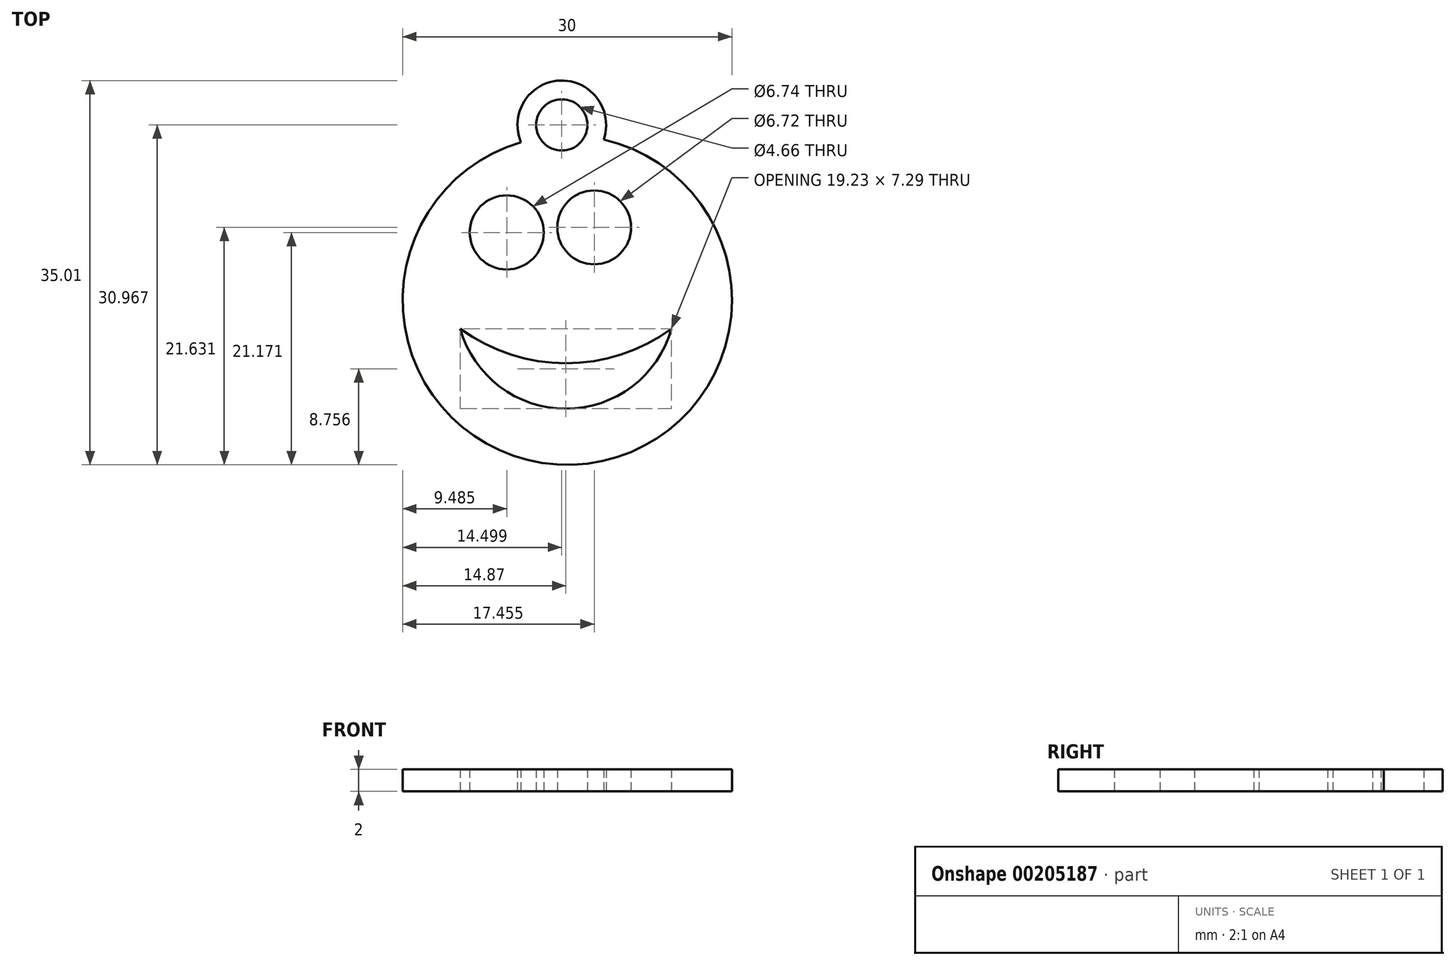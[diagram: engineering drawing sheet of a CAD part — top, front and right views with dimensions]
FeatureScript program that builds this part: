
annotation { "Feature Type Name" : "Feature", "Feature Type Description" : "" }
export const myFeature = defineFeature(function(context is Context, id is Id, definition is map)
    precondition{}
    {
        {
            var Q0;
            Q0=qCreatedBy(makeId("Top.planeOp"),FACE);
            var sketch = newSketch(context, id + "F0", { "sketchPlane" : qUnion([Q0])});
            skArc(sketch, "E0", {"start": v(-4.22, 14.4) * mm, "mid": v(0.47, -15) * mm, "end": v(3.31, 14.63) * mm});
            skArc(sketch, "E1", {"start": v(-9.75, -2.6) * mm, "mid": v(-0.13, -9.89) * mm, "end": v(9.49, -2.6) * mm});
            skArc(sketch, "E2", {"start": v(-9.75, -2.6) * mm, "mid": v(-0.13, -5.75) * mm, "end": v(9.49, -2.6) * mm});
            skCircle(sketch, "E3", {"center": v(-5.52, 6.17) * mm, "radius": 3.37 * mm});
            skCircle(sketch, "E4", {"center": v(2.46, 6.63) * mm, "radius": 3.36 * mm});
            skArc(sketch, "E5", {"start": v(3.31, 14.63) * mm, "mid": v(-0.63, 20) * mm, "end": v(-4.22, 14.4) * mm});
            skCircle(sketch, "E6", {"center": v(-0.5, 15.97) * mm, "radius": 2.33 * mm});
            skSolve(sketch);
        }
        {
            var Q0;
            Q0=makeQuery(id+"F0.imprint","IMPRINT",FACE,{"disambiguationData":[TD([[makeQuery(id+"F0.imprint","IMPRINT",EDGE,{"derivedFrom":sQuery(id+"F0.wireOp",EDGE,"E0")}),1.0]])]});
            extrude(context, id + "F1", {"entities" : qUnion([Q0]), "depth" : 2 * mm});
        }
    });
